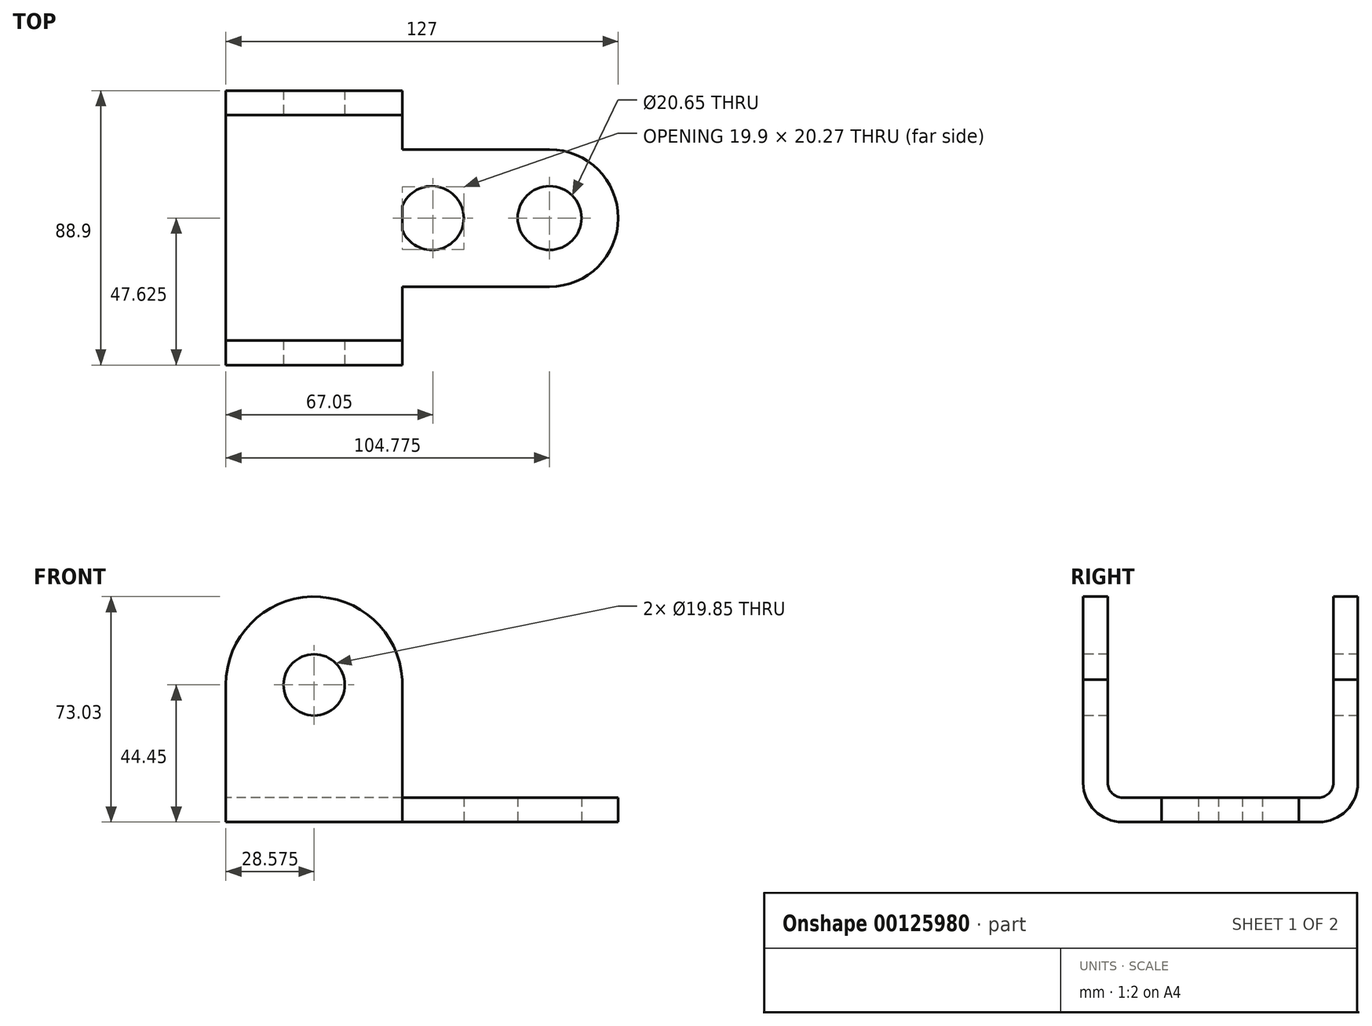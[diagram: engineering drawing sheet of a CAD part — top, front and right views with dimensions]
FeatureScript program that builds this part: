
annotation { "Feature Type Name" : "Feature", "Feature Type Description" : "" }
export const myFeature = defineFeature(function(context is Context, id is Id, definition is map)
    precondition{}
    {
        {
            var Q0;
            Q0=qCreatedBy(makeId("Top.planeOp"),FACE);
            var sketch = newSketch(context, id + "F0", { "sketchPlane" : qUnion([Q0])});
            skLineSegment(sketch, "E0", {"start": v(0, 0) * mm, "end": v(50.8, 0) * mm});
            skLineSegment(sketch, "E1", {"start": v(0, 0) * mm, "end": v(0, 88.9) * mm});
            skLineSegment(sketch, "E2", {"start": v(0, 88.9) * mm, "end": v(50.8, 88.9) * mm});
            skLineSegment(sketch, "E3", {"start": v(50.8, 88.9) * mm, "end": v(50.8, 76.2) * mm});
            skLineSegment(sketch, "E4", {"start": v(50.8, 0) * mm, "end": v(50.8, 19.05) * mm});
            skLineSegment(sketch, "E5", {"start": v(57.15, 69.85) * mm, "end": v(104.78, 69.85) * mm});
            skPoint(sketch, "E6.visualSharp", {"position": v(50.8, 69.85) * mm});
            skArc(sketch, "E6.filletArc", {"start": v(50.8, 76.2) * mm, "mid": v(52.66, 71.7) * mm, "end": v(57.15, 69.85) * mm});
            skLineSegment(sketch, "E7", {"start": v(57.15, 25.4) * mm, "end": v(104.77, 25.4) * mm});
            skPoint(sketch, "E8.visualSharp", {"position": v(50.8, 25.4) * mm});
            skArc(sketch, "E8.filletArc", {"start": v(57.15, 25.4) * mm, "mid": v(52.66, 23.54) * mm, "end": v(50.8, 19.05) * mm});
            skCircle(sketch, "E9", {"center": v(66.67, 47.63) * mm, "radius": 10.33 * mm});
            skCircle(sketch, "E10", {"center": v(104.77, 47.63) * mm, "radius": 10.33 * mm});
            skArc(sketch, "E11", {"start": v(104.77, 25.4) * mm, "mid": v(127, 47.63) * mm, "end": v(104.78, 69.85) * mm});
            skSolve(sketch);
        }
        {
            var Q0;
            Q0 = qSketchRegion(id + "F0", true);
            extrude(context, id + "F1", {"entities" : qUnion([Q0]), "depth" : 7.94 * mm});
        }
        {
            var Q0;
            Q0=qCreatedBy(makeId("Right.planeOp"),FACE);
            var sketch = newSketch(context, id + "F2", { "sketchPlane" : qUnion([Q0])});
            skLineSegment(sketch, "E12", {"start": v(0, 12.7) * mm, "end": v(0, 76.2) * mm});
            skLineSegment(sketch, "E13", {"start": v(88.9, 12.7) * mm, "end": v(88.9, 76.2) * mm});
            skLineSegment(sketch, "E14", {"start": v(0, 76.2) * mm, "end": v(7.94, 76.2) * mm});
            skLineSegment(sketch, "E15", {"start": v(7.94, 76.2) * mm, "end": v(7.94, 12.7) * mm});
            skLineSegment(sketch, "E16", {"start": v(12.7, 7.94) * mm, "end": v(76.2, 7.94) * mm});
            skLineSegment(sketch, "E17", {"start": v(80.96, 12.7) * mm, "end": v(80.96, 76.2) * mm});
            skLineSegment(sketch, "E18", {"start": v(80.96, 76.2) * mm, "end": v(88.9, 76.2) * mm});
            skPoint(sketch, "E19.visualSharp", {"position": v(7.94, 7.94) * mm});
            skArc(sketch, "E19.filletArc", {"start": v(7.94, 12.7) * mm, "mid": v(9.33, 9.33) * mm, "end": v(12.7, 7.94) * mm});
            skPoint(sketch, "E20.visualSharp", {"position": v(80.96, 7.94) * mm});
            skArc(sketch, "E20.filletArc", {"start": v(76.2, 7.94) * mm, "mid": v(79.57, 9.33) * mm, "end": v(80.96, 12.7) * mm});
            skLineSegment(sketch, "E21", {"start": v(12.7, 0) * mm, "end": v(76.2, 0) * mm});
            skPoint(sketch, "E22.visualSharp", {"position": v(0, 0) * mm});
            skArc(sketch, "E22.filletArc", {"start": v(0, 12.7) * mm, "mid": v(3.72, 3.72) * mm, "end": v(12.7, 0) * mm});
            skPoint(sketch, "E23.visualSharp", {"position": v(88.9, 0) * mm});
            skArc(sketch, "E23.filletArc", {"start": v(76.2, 0) * mm, "mid": v(85.18, 3.72) * mm, "end": v(88.9, 12.7) * mm});
            skSolve(sketch);
        }
        {
            var Q0;
            Q0 = qSketchRegion(id + "F2", true);
            extrude(context, id + "F3", {"entities" : qUnion([Q0]), "operationType" : NewBodyOperationType.ADD, "depth" : 57.1 * mm});
        }
        {
            var Q0;
            Q0=qCreatedBy(makeId("Front.planeOp"),FACE);
            var sketch = newSketch(context, id + "F4", { "sketchPlane" : qUnion([Q0])});
            skCircle(sketch, "E24", {"center": v(28.58, 44.45) * mm, "radius": 9.92 * mm});
            skArc(sketch, "E25", {"start": v(57.1, 42.9) * mm, "mid": v(29.35, 73.01) * mm, "end": v(0, 44.45) * mm});
            skLineSegment(sketch, "E26", {"start": v(0, 44.45) * mm, "end": v(0, 76.2) * mm});
            skLineSegment(sketch, "E27", {"start": v(0, 76.2) * mm, "end": v(57.1, 76.2) * mm});
            skLineSegment(sketch, "E28", {"start": v(57.1, 76.2) * mm, "end": v(57.1, 42.9) * mm});
            skSolve(sketch);
        }
        {
            var Q0;
            Q0 = qSketchRegion(id + "F4", true);
            extrude(context, id + "F5", {"entities" : qUnion([Q0]), "operationType" : NewBodyOperationType.REMOVE, "endBound" : BoundingType.THROUGH_ALL, "oppositeDirection" : true, "depth" : 25.4 * mm});
        }
        {
            var Q0;
            Q0=qCreatedBy(makeId("Right.planeOp"),FACE);
            var sketch = newSketch(context, id + "F6", { "sketchPlane" : qUnion([Q0])});
            skLineSegment(sketch, "E29", {"start": v(0, 0) * mm, "end": v(12.7, 0) * mm});
            skLineSegment(sketch, "E30", {"start": v(0, 0) * mm, "end": v(0, 12.7) * mm});
            skLineSegment(sketch, "E31", {"start": v(88.9, 0) * mm, "end": v(76.2, 0) * mm});
            skLineSegment(sketch, "E32", {"start": v(88.9, 0) * mm, "end": v(88.9, 12.7) * mm});
            skArc(sketch, "E33", {"start": v(0, 12.7) * mm, "mid": v(3.72, 3.72) * mm, "end": v(12.7, 0) * mm});
            skArc(sketch, "E34", {"start": v(76.2, 0) * mm, "mid": v(85.18, 3.72) * mm, "end": v(88.9, 12.7) * mm});
            skSolve(sketch);
        }
        {
            var Q0;
            Q0 = qSketchRegion(id + "F6", true);
            extrude(context, id + "F7", {"entities" : qUnion([Q0]), "operationType" : NewBodyOperationType.REMOVE, "endBound" : BoundingType.THROUGH_ALL, "depth" : 25.4 * mm});
        }
    });
